# Revit family: Diverter_Valve-Trim-Delta-Tesla-11X52
name_source: partatom
category: Plumbing Fixtures
revit_build: Autodesk Revit MEP 2012 (Build: 20110916_2132(x64)
units: mm (PartAtom-declared; Revit-internal decimal feet)

## types (2) — shared parameters
Date Modified = January 5, 2015
Default Elevation = 48 "
Equipment Abbreviation = CSD
Family Version = 1.0
Fixture Flow = 0 GPM
Manufacturer = Delta Faucet Company
Model Disclaimer = Contact Delta Faucet Company for More Information
Pipe Size = 0.5 "
Product Material = Steel - Delta Faucet Company - Stainless
URL = http://www.deltafaucet.com
zz Length 1 = 4 "
zz Length 2 = 4.5 "
zz Length 3 = 4.5 "

## per-type parameters (varying)
| type | Description | Model | zz Integer 1 |
| Three Function | Tesla Three Function Custom Shower Diverter | 11852 | 1 |
| Six Function | Tesla Six Function Custom Shower Diverter | 11952 | 2 |

## geometry (parser evidence)
native form markers: Blend x2, Sweep x2
no freeform markers — native parametric forms only
